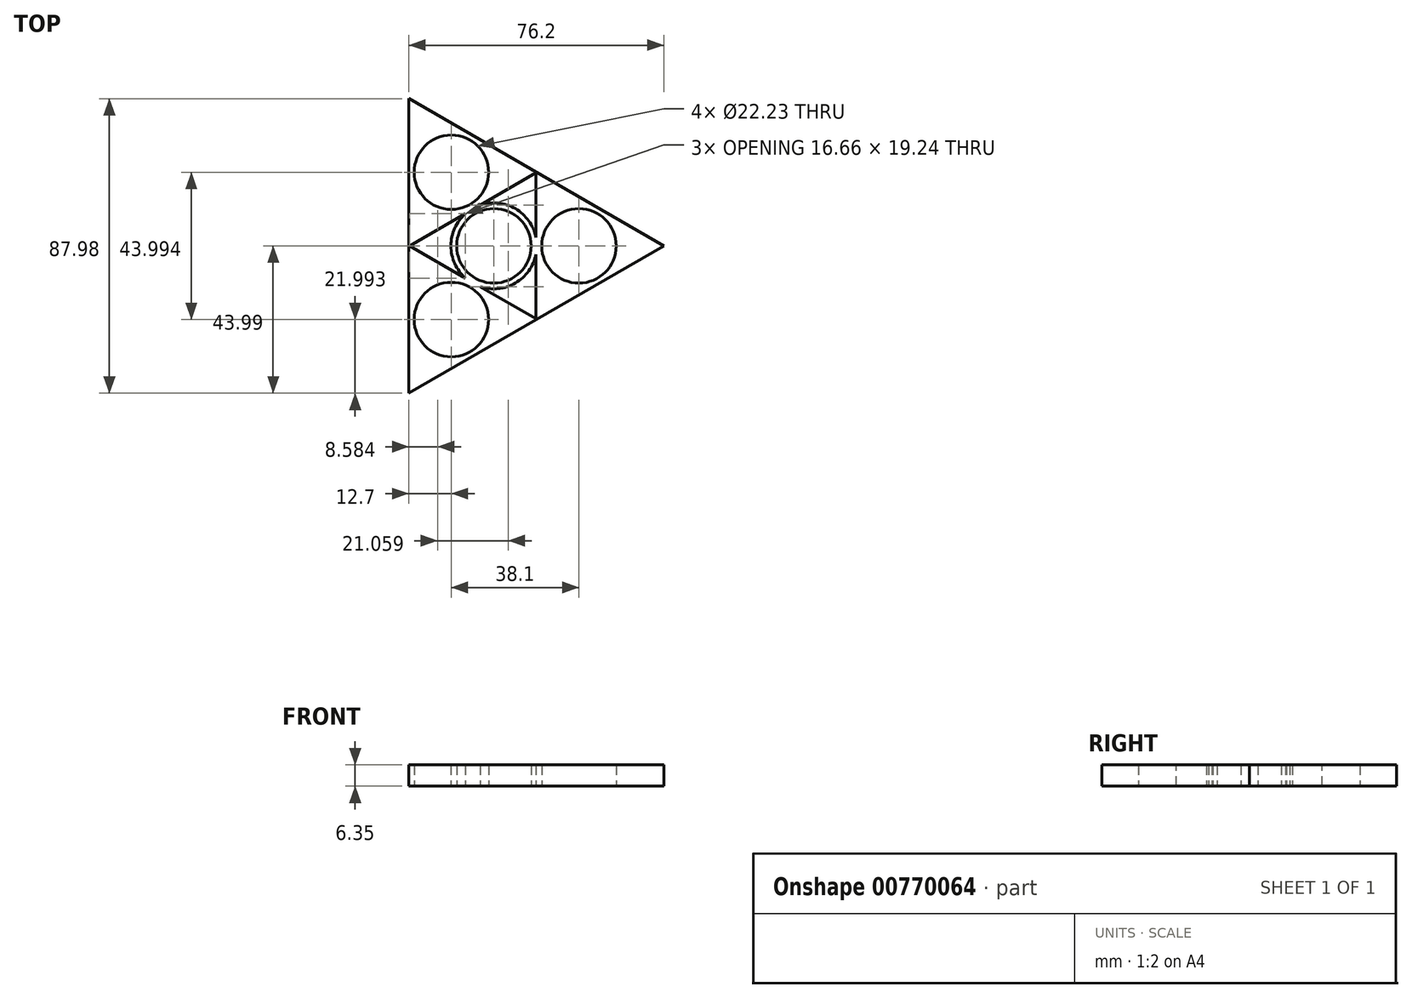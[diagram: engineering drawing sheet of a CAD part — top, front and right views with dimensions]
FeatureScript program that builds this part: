
annotation { "Feature Type Name" : "Feature", "Feature Type Description" : "" }
export const myFeature = defineFeature(function(context is Context, id is Id, definition is map)
    precondition{}
    {
        {
            var Q0;
            Q0=qCreatedBy(makeId("Top.planeOp"),FACE);
            var sketch = newSketch(context, id + "F0", { "sketchPlane" : qUnion([Q0])});
            skCircle(sketch, "E0.cCircle", {"center": v(0, 0) * mm, "radius": 12.7 * mm, "construction": true});
            skLineSegment(sketch, "E0.0", {"start": v(12.7, 22) * mm, "end": v(12.7, -22) * mm});
            skLineSegment(sketch, "E0.2", {"start": v(-25.4, 0) * mm, "end": v(12.7, 22) * mm});
            skPoint(sketch, "E0.0.midPoint", {"position": v(12.7, 0) * mm});
            skLineSegment(sketch, "E1", {"start": v(0, 0) * mm, "end": v(-12.7, -22) * mm});
            skLineSegment(sketch, "E2", {"start": v(0, 0) * mm, "end": v(25.4, 0) * mm});
            skLineSegment(sketch, "E3", {"start": v(0, 0) * mm, "end": v(-12.7, 22) * mm});
            skCircle(sketch, "E4.cCircle", {"center": v(-12.7, 22) * mm, "radius": 12.7 * mm, "construction": true});
            skLineSegment(sketch, "E4.1", {"start": v(-25.4, 0) * mm, "end": v(-25.4, 44) * mm});
            skLineSegment(sketch, "E4.2", {"start": v(-25.4, 44) * mm, "end": v(12.7, 22) * mm});
            skPoint(sketch, "E4.0.midPoint", {"position": v(-6.35, 11) * mm});
            skCircle(sketch, "E5.cCircle", {"center": v(25.4, 0) * mm, "radius": 12.7 * mm, "construction": true});
            skLineSegment(sketch, "E5.1", {"start": v(12.7, 22) * mm, "end": v(50.8, 0) * mm});
            skLineSegment(sketch, "E5.2", {"start": v(50.8, 0) * mm, "end": v(12.7, -22) * mm});
            skCircle(sketch, "E6.cCircle", {"center": v(-12.7, -22) * mm, "radius": 12.7 * mm, "construction": true});
            skLineSegment(sketch, "E6.0", {"start": v(-25.4, 0) * mm, "end": v(12.7, -22) * mm});
            skLineSegment(sketch, "E6.1", {"start": v(12.7, -22) * mm, "end": v(-25.4, -44) * mm});
            skLineSegment(sketch, "E6.2", {"start": v(-25.4, -44) * mm, "end": v(-25.4, 0) * mm});
            skPoint(sketch, "E6.0.midPoint", {"position": v(-6.35, -11) * mm});
            skCircle(sketch, "E7", {"center": v(-12.7, 22) * mm, "radius": 11.11 * mm});
            skCircle(sketch, "E8", {"center": v(25.4, 0) * mm, "radius": 11.11 * mm});
            skCircle(sketch, "E9", {"center": v(-12.7, -22) * mm, "radius": 11.11 * mm});
            skCircle(sketch, "E10", {"center": v(0, 0) * mm, "radius": 11.11 * mm});
            skSolve(sketch);
        }
        {
            var Q0;
            Q0 = qSketchRegion(id + "F0", true);
            extrude(context, id + "F1", {"entities" : qUnion([Q0]), "depth" : 6.35 * mm, "offsetDistance" : 25.4 * mm});
        }
        {
            var Q0;
            Q0=makeQuery(id+"F1.opExtrude","CAP_FACE",FACE,{"disambiguationData":[OSD([sQuery(id+"F0.wireOp",EDGE,"E4.1"),sQuery(id+"F0.wireOp",EDGE,"E4.2"),sQuery(id+"F0.wireOp",EDGE,"E5.1"),sQuery(id+"F0.wireOp",EDGE,"E5.2"),sQuery(id+"F0.wireOp",EDGE,"E6.1"),sQuery(id+"F0.wireOp",EDGE,"E6.2"),sQuery(id+"F0.wireOp",EDGE,"E7"),sQuery(id+"F0.wireOp",EDGE,"E8"),sQuery(id+"F0.wireOp",EDGE,"E9"),sQuery(id+"F0.wireOp",EDGE,"E10")])],"isStart":false});
            var sketch = newSketch(context, id + "F2", { "sketchPlane" : qUnion([Q0])});
            skPoint(sketch, "E11.0.midPoint", {"position": v(11.11, 0) * mm});
            skPoint(sketch, "E12.0.midPoint", {"position": v(12.57, 0) * mm});
            skCircle(sketch, "E13.cCircle", {"center": v(0, 0) * mm, "radius": 11.44 * mm, "construction": true});
            skLineSegment(sketch, "E13.0", {"start": v(11.44, 19.81) * mm, "end": v(11.44, -19.81) * mm});
            skLineSegment(sketch, "E13.1", {"start": v(11.44, -19.81) * mm, "end": v(-22.88, 0) * mm});
            skLineSegment(sketch, "E13.2", {"start": v(-22.88, 0) * mm, "end": v(11.44, 19.81) * mm});
            skPoint(sketch, "E13.0.midPoint", {"position": v(11.44, 0) * mm});
            skCircle(sketch, "E14.cCircle", {"center": v(0, 0) * mm, "radius": 12.57 * mm, "construction": true});
            skLineSegment(sketch, "E14.0", {"start": v(12.57, 21.78) * mm, "end": v(12.57, -21.78) * mm});
            skLineSegment(sketch, "E14.1", {"start": v(12.57, -21.78) * mm, "end": v(-25.15, 0) * mm});
            skLineSegment(sketch, "E14.2", {"start": v(-25.15, 0) * mm, "end": v(12.57, 21.78) * mm});
            skSolve(sketch);
        }
        {
            var Q0;
            Q0 = qSketchRegion(id + "F2", true);
            extrude(context, id + "F3", {"entities" : qUnion([Q0]), "operationType" : NewBodyOperationType.REMOVE, "oppositeDirection" : true, "depth" : 1.27 * mm, "offsetDistance" : 25.4 * mm});
        }
        {
            var Q0;
            Q0=makeQuery(id+"F1.opExtrude","CAP_FACE",FACE,{"disambiguationData":[OSD([sQuery(id+"F0.wireOp",EDGE,"E4.1"),sQuery(id+"F0.wireOp",EDGE,"E4.2"),sQuery(id+"F0.wireOp",EDGE,"E5.1"),sQuery(id+"F0.wireOp",EDGE,"E5.2"),sQuery(id+"F0.wireOp",EDGE,"E6.1"),sQuery(id+"F0.wireOp",EDGE,"E6.2"),sQuery(id+"F0.wireOp",EDGE,"E7"),sQuery(id+"F0.wireOp",EDGE,"E8"),sQuery(id+"F0.wireOp",EDGE,"E9"),sQuery(id+"F0.wireOp",EDGE,"E10")])],"isStart":true});
            var sketch = newSketch(context, id + "F4", { "sketchPlane" : qUnion([Q0])});
            skPoint(sketch, "E15.0.midPoint", {"position": v(11.43, 0) * mm});
            skCircle(sketch, "E16.cCircle", {"center": v(0, 0) * mm, "radius": 12.57 * mm, "construction": true});
            skLineSegment(sketch, "E16.0", {"start": v(12.57, 21.78) * mm, "end": v(12.57, -21.78) * mm});
            skLineSegment(sketch, "E16.1", {"start": v(12.57, -21.78) * mm, "end": v(-25.15, 0) * mm});
            skLineSegment(sketch, "E16.2", {"start": v(-25.15, 0) * mm, "end": v(12.57, 21.78) * mm});
            skPoint(sketch, "E16.0.midPoint", {"position": v(12.57, 0) * mm});
            skCircle(sketch, "E17", {"center": v(0, 0) * mm, "radius": 12.83 * mm});
            skSolve(sketch);
        }
        {
            var Q0;
            Q0 = qSketchRegion(id + "F4", true);
            extrude(context, id + "F5", {"entities" : qUnion([Q0]), "operationType" : NewBodyOperationType.REMOVE, "oppositeDirection" : true, "depth" : 6.35 * mm, "offsetDistance" : 25.4 * mm});
        }
        {
            var Q0;
            Q0=makeQuery(id+"F1.opExtrude","CAP_FACE",FACE,{"disambiguationData":[OSD([sQuery(id+"F0.wireOp",EDGE,"E4.1"),sQuery(id+"F0.wireOp",EDGE,"E4.2"),sQuery(id+"F0.wireOp",EDGE,"E5.1"),sQuery(id+"F0.wireOp",EDGE,"E5.2"),sQuery(id+"F0.wireOp",EDGE,"E6.1"),sQuery(id+"F0.wireOp",EDGE,"E6.2"),sQuery(id+"F0.wireOp",EDGE,"E7"),sQuery(id+"F0.wireOp",EDGE,"E8"),sQuery(id+"F0.wireOp",EDGE,"E9"),sQuery(id+"F0.wireOp",EDGE,"E10")])],"isStart":true});
            var sketch = newSketch(context, id + "F6", { "sketchPlane" : qUnion([Q0])});
            skCircle(sketch, "E18", {"center": v(0, 0) * mm, "radius": 12.83 * mm});
            skCircle(sketch, "E19", {"center": v(0, 0) * mm, "radius": 11.11 * mm});
            skSolve(sketch);
        }
        {
            var Q0;
            Q0 = qSketchRegion(id + "F6", true);
            extrude(context, id + "F7", {"entities" : qUnion([Q0]), "operationType" : NewBodyOperationType.ADD, "oppositeDirection" : true, "depth" : 6.35 * mm, "offsetDistance" : 25.4 * mm});
        }
    });
